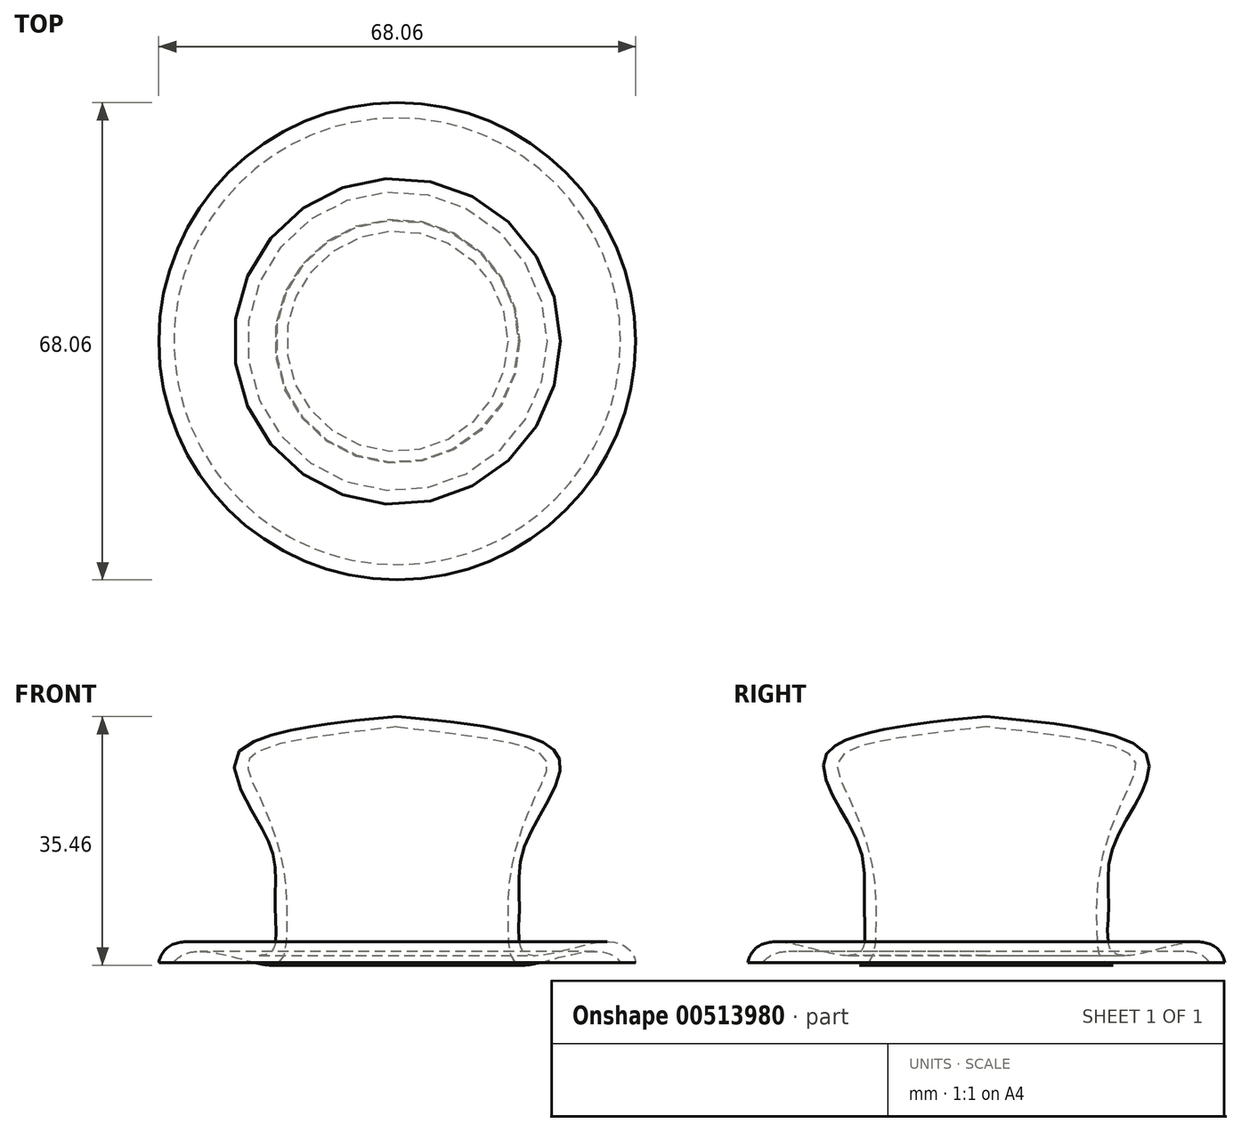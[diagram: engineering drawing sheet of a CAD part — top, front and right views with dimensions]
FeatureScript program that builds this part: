
annotation { "Feature Type Name" : "Feature", "Feature Type Description" : "" }
export const myFeature = defineFeature(function(context is Context, id is Id, definition is map)
    precondition{}
    {
        {
            var Q0;
            Q0=qCreatedBy(makeId("Front.planeOp"),FACE);
            var sketch = newSketch(context, id + "F0", { "sketchPlane" : qUnion([Q0])});
            skFitSpline(sketch, "E0", {"points": [v(0, 33.78) * mm, v(9.96, 32.72) * mm, v(17.96, 31.12) * mm, v(22.94, 28.27) * mm, v(22.05, 22.76) * mm, v(17.78, 14.22) * mm, v(17.42, 6.05) * mm, v(18.31, 0) * mm, v(28.98, 1.6) * mm, v(33.52, 0) * mm, v(33.34, -3.59) * mm, v(17.5, -5.34) * mm, v(0, -5.37) * mm], "startDerivative": vector(112.3, -10.52) * mm, "endDerivative": vector(-135.62, -1.64) * mm});
            skPoint(sketch, "E1.endSnap0", {"position": v(0, 14.2) * mm});
            skFitSpline(sketch, "E2", {"points": [v(0, 32.3) * mm, v(11.36, 30.9) * mm, v(21.06, 27.79) * mm, v(19.93, 22.89) * mm, v(16.35, 12.72) * mm, v(15.78, 3.67) * mm, v(16.73, -1.22) * mm, v(20.68, -1.22) * mm, v(30.1, 0) * mm, v(32.17, -2.73) * mm, v(24.54, -4.52) * mm, v(5.14, -3.86) * mm, v(0, -3.58) * mm], "startDerivative": vector(106.54, -11.78) * mm, "endDerivative": vector(-61.42, 3.2) * mm});
            skLineSegment(sketch, "E3", {"start": v(0, 33.78) * mm, "end": v(0, 32.3) * mm});
            skLineSegment(sketch, "E4", {"start": v(0, 38.5) * mm, "end": v(0, -3.58) * mm, "construction": true});
            skLineSegment(sketch, "E5", {"start": v(34.03, -1.32) * mm, "end": v(31.86, -1.32) * mm});
            skLineSegment(sketch, "E6.trimOffspring", {"start": v(0, -5.37) * mm, "end": v(0, -13.57) * mm, "construction": true});
            skSolve(sketch);
        }
        {
            var Q0;
            Q0=makeQuery(id+"F0.imprint","IMPRINT",FACE,{"disambiguationData":[TD([[makeQuery(id+"F0.imprint","IMPRINT",EDGE,{"derivedFrom":sQuery(id+"F0.wireOp",EDGE,"E0")}),-1.0]])]});
            var Q1;
            Q1=sQuery(id+"F0.wireOp",EDGE,"E1");
            var Q2;
            Q2=sQuery(id+"F0.wireOp",EDGE,"E4");
            revolve(context, id + "F1", {"entities" : qUnion([Q0]), "surfaceEntities" : qUnion([Q1]), "axis" : qUnion([Q2]), "revolveType" : RevolveType.FULL});
        }
    });
